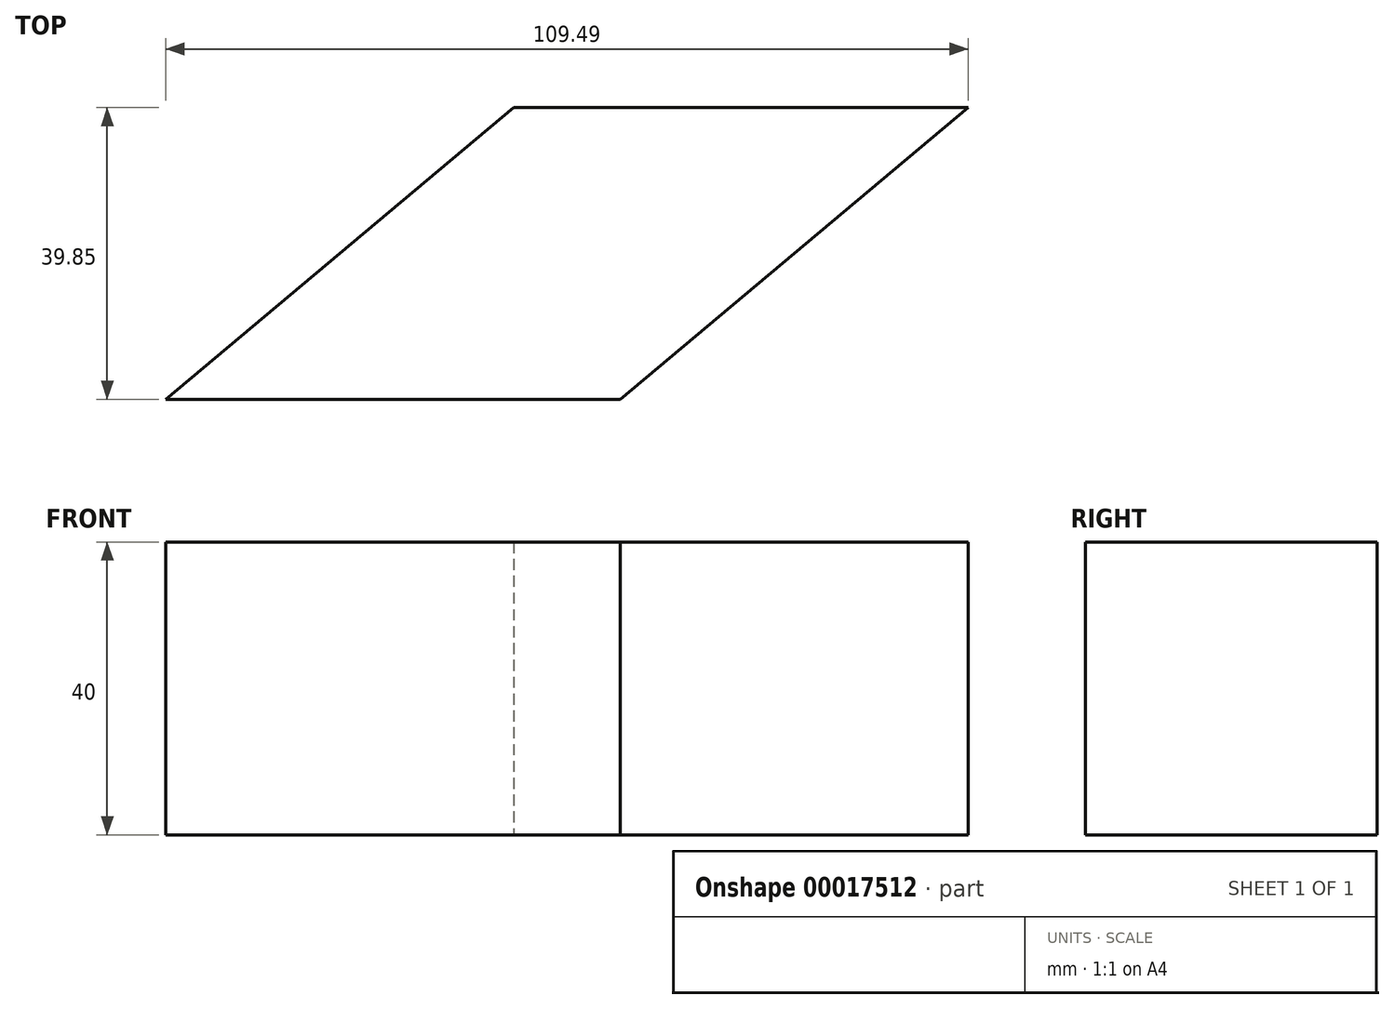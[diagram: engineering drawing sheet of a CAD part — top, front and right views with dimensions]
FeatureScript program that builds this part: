
annotation { "Feature Type Name" : "Feature", "Feature Type Description" : "" }
export const myFeature = defineFeature(function(context is Context, id is Id, definition is map)
    precondition{}
    {
        {
            var Q0;
            Q0=qCreatedBy(makeId("Top.planeOp"),FACE);
            var sketch = newSketch(context, id + "F0", { "sketchPlane" : qUnion([Q0])});
            skLineSegment(sketch, "E0", {"start": v(-47.5, 0) * mm, "end": v(0, 39.85) * mm});
            skLineSegment(sketch, "E1", {"start": v(0, 39.85) * mm, "end": v(62, 39.85) * mm});
            skLineSegment(sketch, "E2", {"start": v(62, 39.85) * mm, "end": v(14.5, 0) * mm});
            skLineSegment(sketch, "E3", {"start": v(14.5, 0) * mm, "end": v(-47.5, 0) * mm});
            skSolve(sketch);
        }
        {
            var Q0;
            Q0=makeQuery(id+"F0.imprint","IMPRINT",FACE,{"disambiguationData":[TD([[makeQuery(id+"F0.imprint","IMPRINT",EDGE,{"derivedFrom":sQuery(id+"F0.wireOp",EDGE,"E0")}),-1.0]])]});
            extrude(context, id + "F1", {"entities" : qUnion([Q0]), "depth" : 40 * mm});
        }
    });
